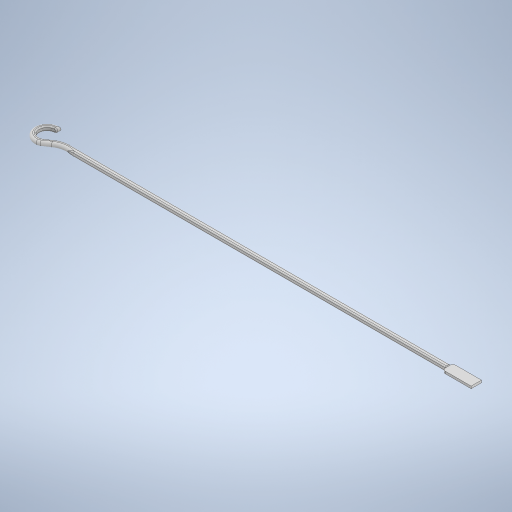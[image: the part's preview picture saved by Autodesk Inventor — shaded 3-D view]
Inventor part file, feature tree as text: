
AUTODESK INVENTOR PART (.ipt)
format: ipt  version: 2024 (Build 280153000, 153)  size: 358,400 bytes
history: native  units: mm
features: extrude x2, other x2, fillet x2, sketch x2
ambient origin geometry x8: Origin, YZ Plane, XZ Plane, XY Plane, X Axis, Y Axis, Z Axis, Center Point
bodies: Solid1 (feature_tree)
feature tree (8):
  extrude  "Extrusion1"  Depth=35.0mm
  other  "Full Round Fillet1"
  other  "Full Round Fillet4"
  extrude  "Extrusion3"  Depth=2.0mm
  fillet  "Fillet2"  Radius=12.5mm
  fillet  "Fillet3"  Radius=8.0mm
  sketch  "Sketch1"  dims[d0=725.0mm d2=35.0mm]
  sketch  "Sketch3"  dims[d3=12.5mm d4=35.0mm d6=12.5mm d7=8.0mm d8=8.0mm d9=8.0mm d10=8.0mm d11=0.0mm d18=5.0mm d19=5.0mm d20=50.0mm d21=5.0mm d22=5.0mm d23=2.0mm d24=2.0mm d25=50.0mm d26=0.0mm d27=2.0mm d28=2.0mm]
